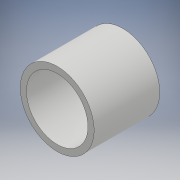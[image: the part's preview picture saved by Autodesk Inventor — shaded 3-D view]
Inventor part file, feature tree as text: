
AUTODESK INVENTOR PART (.ipt)
format: ipt  version: 2018 (Build 220112000, 112)  size: 218,112 bytes
history: native  units: mm
features: extrude x1, sketch x1
ambient origin geometry x8: Origin, YZ Plane, XZ Plane, XY Plane, X Axis, Y Axis, Z Axis, Center Point
bodies: Solid1 (feature_tree)
feature tree (2):
  extrude  "Extrusion1"  Depth=4.0mm
  sketch  "Sketch1"  dims[d0=4.5mm d1=3.75mm d2=4.0mm d3=0.0mm]
